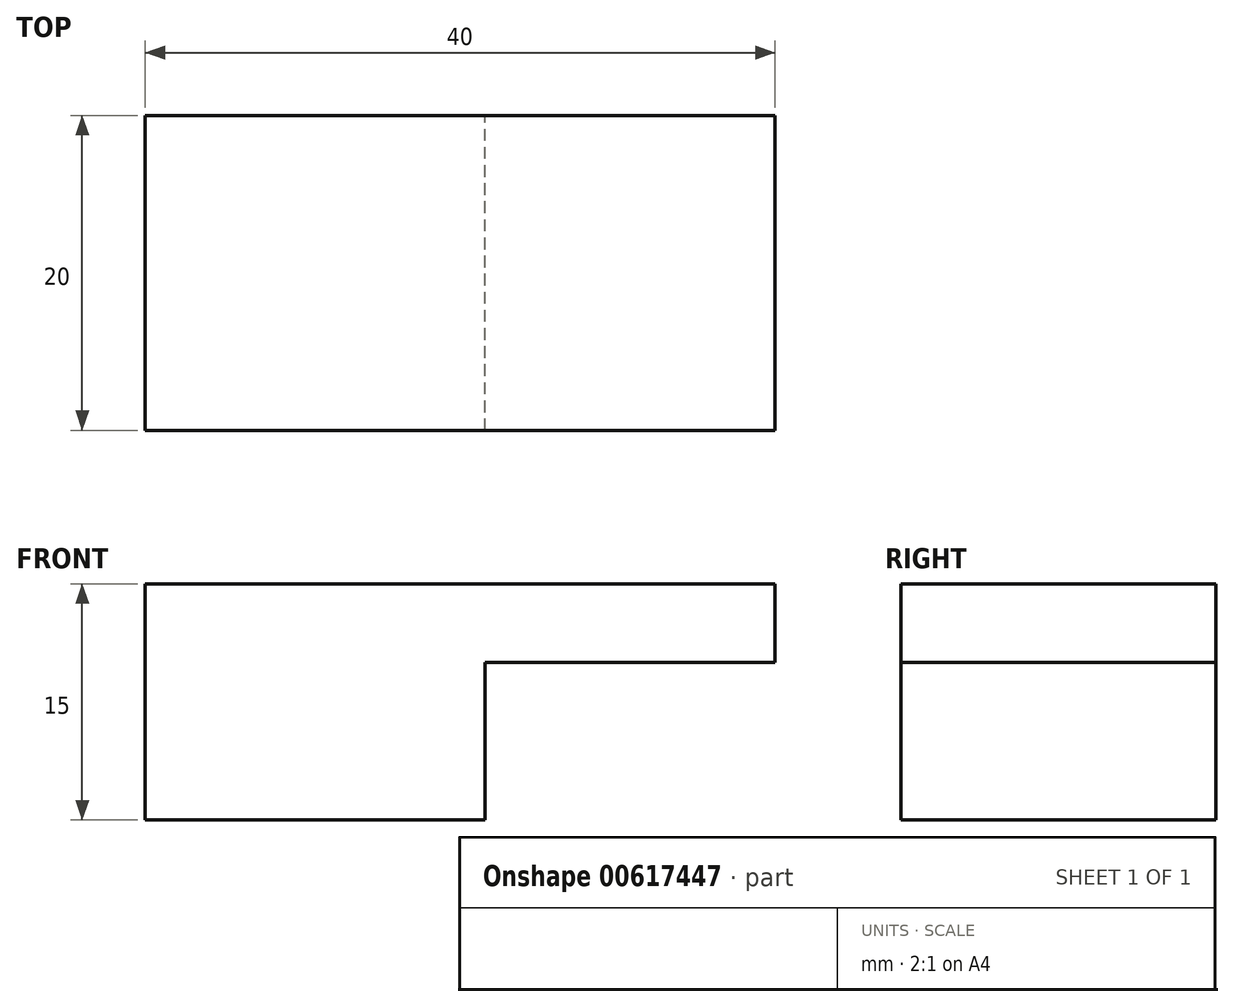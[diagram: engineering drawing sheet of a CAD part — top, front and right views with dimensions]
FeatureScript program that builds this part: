
annotation { "Feature Type Name" : "Feature", "Feature Type Description" : "" }
export const myFeature = defineFeature(function(context is Context, id is Id, definition is map)
    precondition{}
    {
        {
            var Q0;
            Q0=qCreatedBy(makeId("Top.planeOp"),FACE);
            var sketch = newSketch(context, id + "F0", { "sketchPlane" : qUnion([Q0])});
            skLineSegment(sketch, "E0.bottom", {"start": v(-10.8, -10) * mm, "end": v(10.8, -10) * mm});
            skLineSegment(sketch, "E0.top", {"start": v(-10.8, 10) * mm, "end": v(10.8, 10) * mm});
            skLineSegment(sketch, "E0.left", {"start": v(-10.8, -10) * mm, "end": v(-10.8, 10) * mm});
            skLineSegment(sketch, "E0.right", {"start": v(10.8, -10) * mm, "end": v(10.8, 10) * mm});
            skPoint(sketch, "E0.middle", {"position": v(0, 0) * mm});
            skSolve(sketch);
        }
        {
            var Q0;
            Q0=makeQuery(id+"F0.imprint","IMPRINT",FACE,{"disambiguationData":[TD([[makeQuery(id+"F0.imprint","IMPRINT",EDGE,{"derivedFrom":sQuery(id+"F0.wireOp",EDGE,"E0.bottom")}),1.0]])]});
            extrude(context, id + "F1", {"entities" : qUnion([Q0]), "depth" : 10 * mm, "offsetDistance" : 25 * mm});
        }
        {
            var Q0;
            Q0=makeQuery(id+"F1.opExtrude","CAP_FACE",FACE,{"disambiguationData":[OSD([sQuery(id+"F0.wireOp",EDGE,"E0.bottom"),sQuery(id+"F0.wireOp",EDGE,"E0.top"),sQuery(id+"F0.wireOp",EDGE,"E0.left"),sQuery(id+"F0.wireOp",EDGE,"E0.right")])],"isStart":false});
            var sketch = newSketch(context, id + "F2", { "sketchPlane" : qUnion([Q0])});
            skLineSegment(sketch, "E1.bottom", {"start": v(-10.8, 10) * mm, "end": v(29.2, 10) * mm});
            skLineSegment(sketch, "E1.top", {"start": v(-10.8, -10) * mm, "end": v(29.2, -10) * mm});
            skLineSegment(sketch, "E1.left", {"start": v(-10.8, 10) * mm, "end": v(-10.8, -10) * mm});
            skLineSegment(sketch, "E1.right", {"start": v(29.2, 10) * mm, "end": v(29.2, -10) * mm});
            skSolve(sketch);
        }
        {
            var Q0;
            {var subQ2=sQuery(id+"F2.wireOp",EDGE,"E1.right");Q0=makeQuery(id+"F2.imprint","IMPRINT",FACE,{"disambiguationData":[TD([[makeQuery(id+"F2.imprint","IMPRINT",EDGE,{"derivedFrom":subQ2}),-1.0]])]});}
            var Q1;
            {var subQ0=sQuery(id+"F2.wireOp",EDGE,"E1.left");Q1=makeQuery(id+"F2.imprint","IMPRINT",FACE,{"disambiguationData":[TD([[makeQuery(id+"F2.imprint","IMPRINT",EDGE,{"derivedFrom":subQ0}),-1.0]])]});}
            extrude(context, id + "F3", {"entities" : qUnion([Q0, Q1]), "operationType" : NewBodyOperationType.ADD, "depth" : 5 * mm, "offsetDistance" : 25 * mm});
        }
    });
